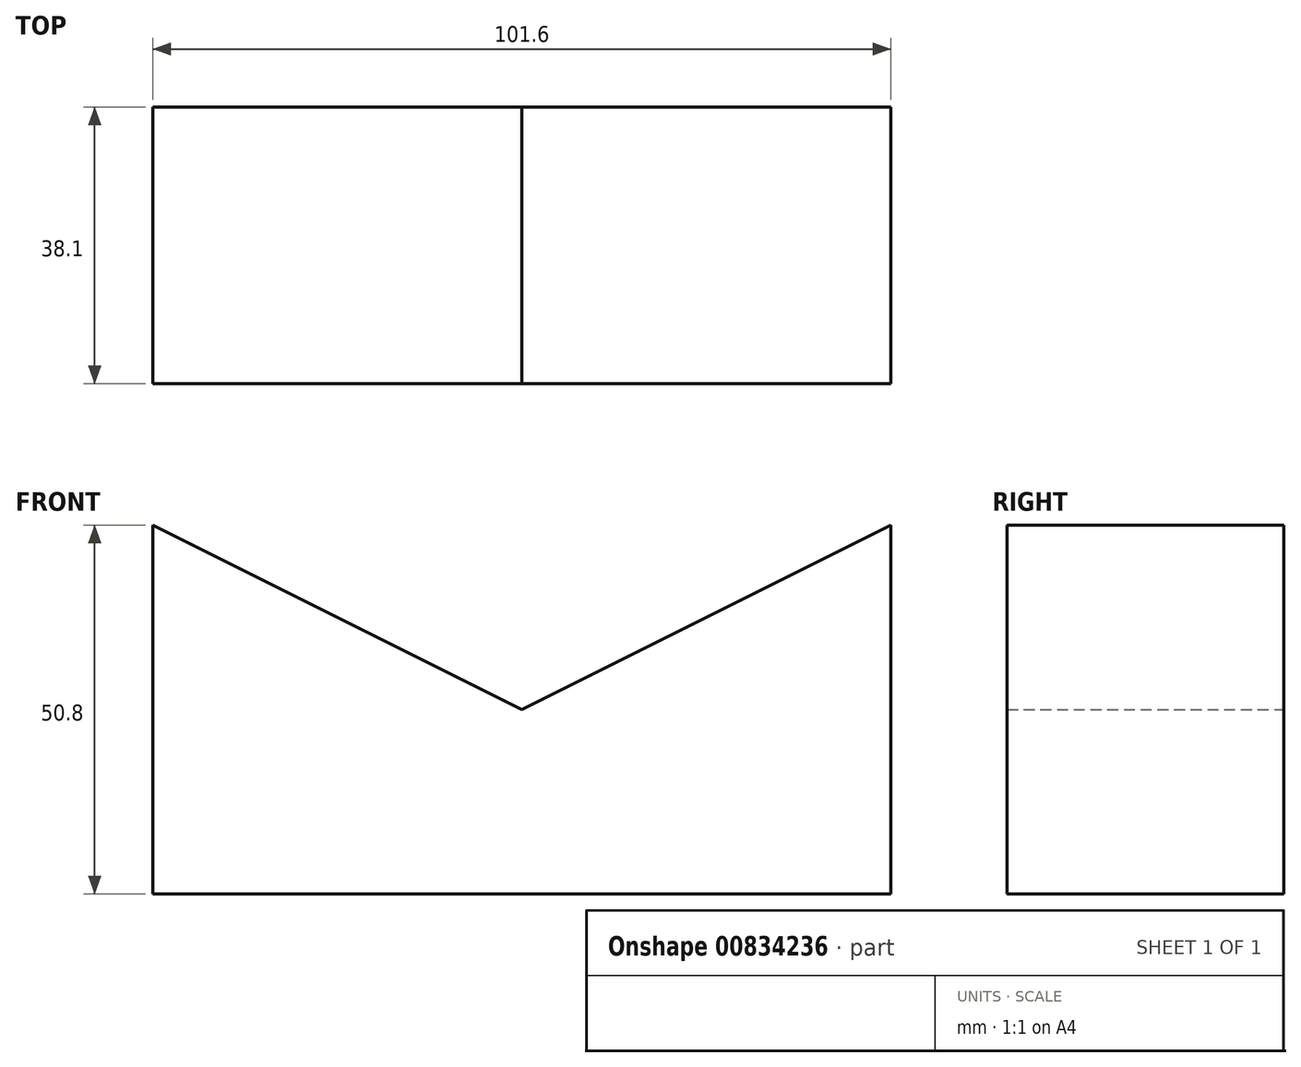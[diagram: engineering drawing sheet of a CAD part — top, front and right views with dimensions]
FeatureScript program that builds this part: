
annotation { "Feature Type Name" : "Feature", "Feature Type Description" : "" }
export const myFeature = defineFeature(function(context is Context, id is Id, definition is map)
    precondition{}
    {
        {
            var Q0;
            Q0=qCreatedBy(makeId("Front.planeOp"),FACE);
            var sketch = newSketch(context, id + "F0", { "sketchPlane" : qUnion([Q0])});
            skLineSegment(sketch, "E0", {"start": v(-50.8, 50.8) * mm, "end": v(-50.8, 0) * mm});
            skLineSegment(sketch, "E1", {"start": v(-50.8, 0) * mm, "end": v(50.8, 0) * mm});
            skLineSegment(sketch, "E2", {"start": v(50.8, 0) * mm, "end": v(50.8, 50.8) * mm});
            skLineSegment(sketch, "E3", {"start": v(50.8, 50.8) * mm, "end": v(0, 25.4) * mm});
            skLineSegment(sketch, "E4", {"start": v(0, 25.4) * mm, "end": v(-50.8, 50.8) * mm});
            skSolve(sketch);
        }
        {
            var Q0;
            Q0=makeQuery(id+"F0.imprint","IMPRINT",FACE,{"disambiguationData":[TD([[makeQuery(id+"F0.imprint","IMPRINT",EDGE,{"derivedFrom":sQuery(id+"F0.wireOp",EDGE,"E0")}),1.0]])]});
            extrude(context, id + "F1", {"entities" : qUnion([Q0]), "depth" : 38.1 * mm, "offsetDistance" : 25.4 * mm});
        }
    });
